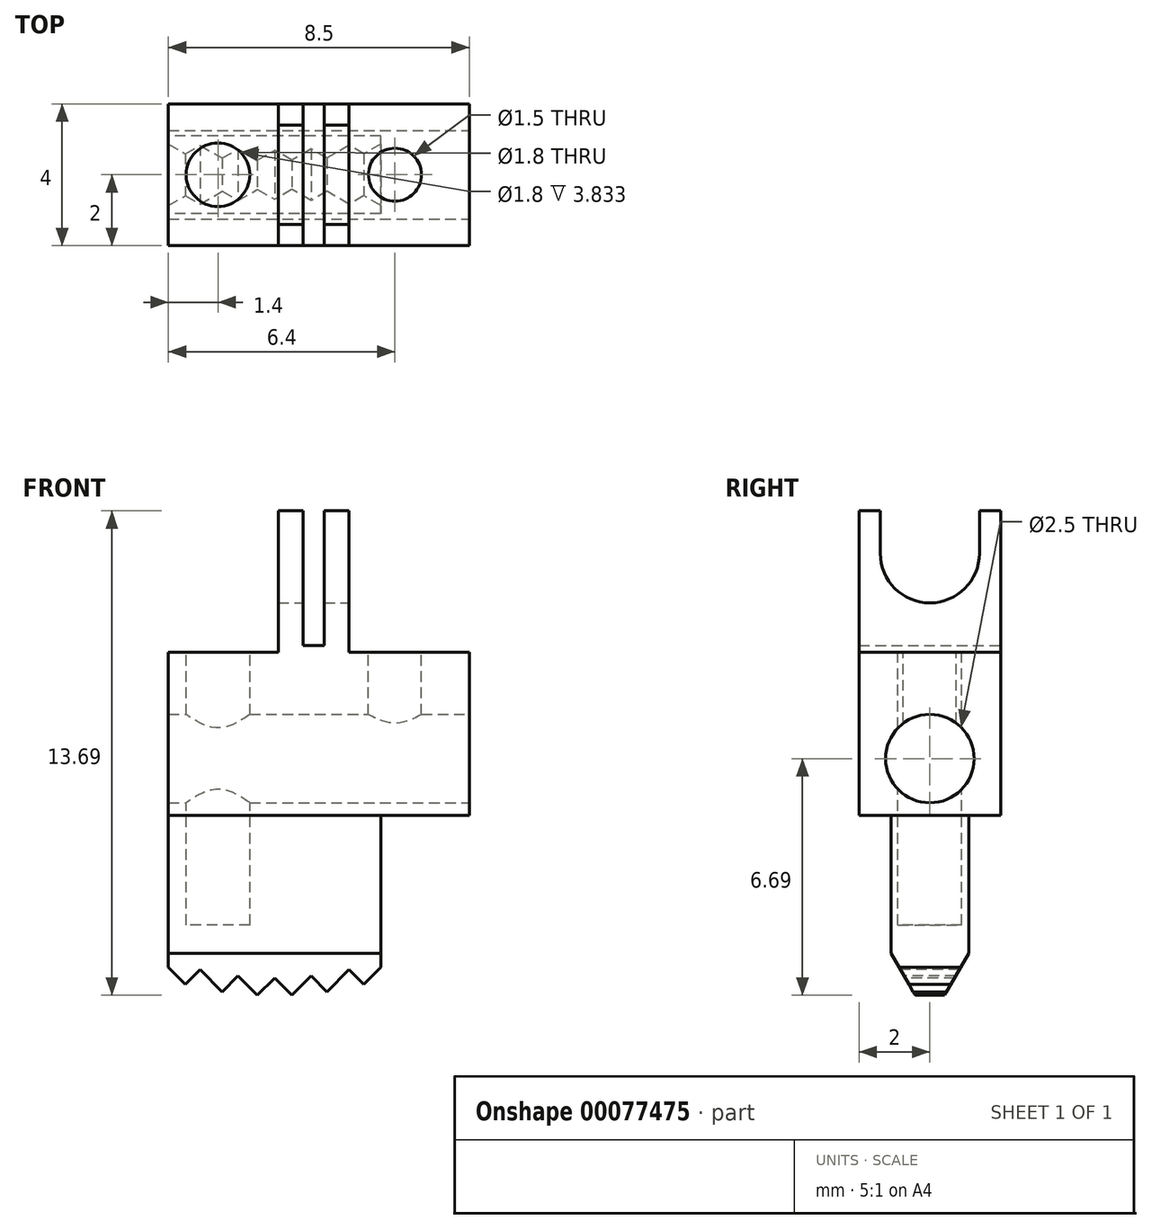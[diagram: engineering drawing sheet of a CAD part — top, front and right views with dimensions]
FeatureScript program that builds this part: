
annotation { "Feature Type Name" : "Feature", "Feature Type Description" : "" }
export const myFeature = defineFeature(function(context is Context, id is Id, definition is map)
    precondition{}
    {
        {
            var Q0;
            Q0=qCreatedBy(makeId("Front.planeOp"),FACE);
            var sketch = newSketch(context, id + "F0", { "sketchPlane" : qUnion([Q0])});
            skLineSegment(sketch, "E0", {"start": v(0, 0) * mm, "end": v(-6, 0) * mm});
            skLineSegment(sketch, "E1", {"start": v(0, 0) * mm, "end": v(0, 5.1) * mm});
            skLineSegment(sketch, "E2", {"start": v(0, 5.1) * mm, "end": v(2.5, 5.1) * mm});
            skLineSegment(sketch, "E3", {"start": v(2.5, 5.1) * mm, "end": v(2.5, 9.7) * mm});
            skLineSegment(sketch, "E4", {"start": v(2.5, 9.7) * mm, "end": v(-0.9, 9.7) * mm});
            skLineSegment(sketch, "E5", {"start": v(-0.9, 9.7) * mm, "end": v(-0.9, 13.7) * mm});
            skLineSegment(sketch, "E6", {"start": v(-0.9, 13.7) * mm, "end": v(-1.6, 13.7) * mm});
            skLineSegment(sketch, "E7", {"start": v(-1.6, 13.7) * mm, "end": v(-1.6, 9.9) * mm});
            skLineSegment(sketch, "E8", {"start": v(-1.6, 9.9) * mm, "end": v(-2.2, 9.9) * mm});
            skLineSegment(sketch, "E9", {"start": v(-2.2, 9.9) * mm, "end": v(-2.2, 13.7) * mm});
            skLineSegment(sketch, "E10", {"start": v(-2.2, 13.7) * mm, "end": v(-2.9, 13.7) * mm});
            skLineSegment(sketch, "E11", {"start": v(-2.9, 13.7) * mm, "end": v(-2.9, 9.7) * mm});
            skLineSegment(sketch, "E12", {"start": v(-2.9, 9.7) * mm, "end": v(-6, 9.7) * mm});
            skLineSegment(sketch, "E13", {"start": v(-6, 9.7) * mm, "end": v(-6, 0) * mm});
            skLineSegment(sketch, "E14", {"start": v(-3, 0) * mm, "end": v(-3, 10) * mm, "construction": true});
            skCircle(sketch, "E15", {"center": v(-3, 10) * mm, "radius": 10 * mm, "construction": true});
            skLineSegment(sketch, "E16", {"start": v(0, 5.1) * mm, "end": v(-6, 5.1) * mm});
            skSolve(sketch);
        }
        {
            var Q0;
            Q0=makeQuery(id+"F0.imprint","IMPRINT",FACE,{"disambiguationData":[TD([[makeQuery(id+"F0.imprint","IMPRINT",EDGE,{"derivedFrom":sQuery(id+"F0.wireOp",EDGE,"E2")}),1.0]])]});
            extrude(context, id + "F1", {"entities" : qUnion([Q0]), "depth" : 4 * mm, "symmetric" : true});
        }
        {
            var Q0;
            {var subQ2=sQuery(id+"F0.wireOp",EDGE,"E0");Q0=makeQuery(id+"F0.imprint","IMPRINT",FACE,{"disambiguationData":[TD([[makeQuery(id+"F0.imprint","IMPRINT",EDGE,{"derivedFrom":subQ2}),-1.0]])]});}
            extrude(context, id + "F2", {"entities" : qUnion([Q0]), "operationType" : NewBodyOperationType.ADD, "depth" : 2.2 * mm, "symmetric" : true});
        }
        {
            var Q0;
            Q0=makeQuery(id+"F1.opExtrude","SWEPT_FACE",FACE,{"disambiguationData":[OSD([sQuery(id+"F0.wireOp",EDGE,"E5")])]});
            var sketch = newSketch(context, id + "F3", { "sketchPlane" : qUnion([Q0])});
            skLineSegment(sketch, "E17", {"start": v(2, 11.1) * mm, "end": v(-2, 11.1) * mm, "construction": true});
            skArc(sketch, "E18", {"start": v(-1.4, 12.5) * mm, "mid": v(0, 11.1) * mm, "end": v(1.4, 12.5) * mm});
            skLineSegment(sketch, "E19", {"start": v(-1.4, 12.5) * mm, "end": v(-1.4, 13.9) * mm});
            skLineSegment(sketch, "E20", {"start": v(-1.4, 13.9) * mm, "end": v(1.4, 13.9) * mm});
            skLineSegment(sketch, "E21", {"start": v(1.4, 13.9) * mm, "end": v(1.4, 12.5) * mm});
            skSolve(sketch);
        }
        {
            var Q0;
            {var subQ5=sQuery(id+"F3.wireOp",EDGE,"E20");Q0=makeQuery(id+"F3.imprint","IMPRINT",FACE,{"disambiguationData":[TD([[makeQuery(id+"F3.imprint","IMPRINT",EDGE,{"derivedFrom":subQ5}),-1.0]])]});}
            var Q1;
            {var subQ5=sQuery(id+"F3.wireOp",EDGE,"E18");Q1=makeQuery(id+"F3.imprint","IMPRINT",FACE,{"disambiguationData":[TD([[makeQuery(id+"F3.imprint","IMPRINT",EDGE,{"derivedFrom":subQ5}),1.0]])]});}
            extrude(context, id + "F4", {"entities" : qUnion([Q0, Q1]), "operationType" : NewBodyOperationType.REMOVE, "oppositeDirection" : true, "depth" : 2 * mm});
        }
        {
            var Q0;
            Q0=makeQuery(id+"F1.opExtrude","SWEPT_FACE",FACE,{"disambiguationData":[OSD([sQuery(id+"F0.wireOp",EDGE,"E3")])]});
            var sketch = newSketch(context, id + "F5", { "sketchPlane" : qUnion([Q0])});
            skLineSegment(sketch, "E22", {"start": v(0, 9.7) * mm, "end": v(0, 6.7) * mm, "construction": true});
            skCircle(sketch, "E23", {"center": v(0, 6.7) * mm, "radius": 1.25 * mm});
            skSolve(sketch);
        }
        {
            var Q0;
            Q0=makeQuery(id+"F5.imprint","IMPRINT",FACE,{"disambiguationData":[TD([[makeQuery(id+"F5.imprint","IMPRINT",EDGE,{"derivedFrom":sQuery(id+"F5.wireOp",EDGE,"E23")}),1.0]])]});
            extrude(context, id + "F6", {"entities" : qUnion([Q0]), "operationType" : NewBodyOperationType.REMOVE, "oppositeDirection" : true, "depth" : 8.5 * mm});
        }
        {
            var Q0;
            Q0=makeQuery(id+"F1.opExtrude","SWEPT_FACE",FACE,{"disambiguationData":[OSD([sQuery(id+"F0.wireOp",EDGE,"E4")])]});
            var sketch = newSketch(context, id + "F7", { "sketchPlane" : qUnion([Q0])});
            skCircle(sketch, "E24", {"center": v(0.4, 0) * mm, "radius": 0.75 * mm});
            skSolve(sketch);
        }
        {
            var Q0;
            Q0=makeQuery(id+"F7.imprint","IMPRINT",FACE,{"disambiguationData":[TD([[makeQuery(id+"F7.imprint","IMPRINT",EDGE,{"derivedFrom":sQuery(id+"F7.wireOp",EDGE,"E24")}),1.0]])]});
            extrude(context, id + "F8", {"entities" : qUnion([Q0]), "operationType" : NewBodyOperationType.REMOVE, "oppositeDirection" : true, "depth" : 3 * mm});
        }
        {
            var Q0;
            Q0=makeQuery(id+"F1.opExtrude","SWEPT_FACE",FACE,{"disambiguationData":[OSD([sQuery(id+"F0.wireOp",EDGE,"E12")])]});
            var sketch = newSketch(context, id + "F9", { "sketchPlane" : qUnion([Q0])});
            skLineSegment(sketch, "E25", {"start": v(-4.6, 2) * mm, "end": v(-4.6, -2) * mm, "construction": true});
            skCircle(sketch, "E26", {"center": v(-4.6, 0) * mm, "radius": 0.9 * mm});
            skSolve(sketch);
        }
        {
            var Q0;
            Q0=makeQuery(id+"F9.imprint","IMPRINT",FACE,{"disambiguationData":[TD([[makeQuery(id+"F9.imprint","IMPRINT",EDGE,{"derivedFrom":sQuery(id+"F9.wireOp",EDGE,"E26")}),1.0]])]});
            extrude(context, id + "F10", {"entities" : qUnion([Q0]), "operationType" : NewBodyOperationType.REMOVE, "oppositeDirection" : true, "depth" : 7.7 * mm});
        }
        {
            var Q0;
            Q0=makeQuery(id+"F2.opExtrude","CAP_EDGE",EDGE,{"disambiguationData":[OSD([sQuery(id+"F0.wireOp",EDGE,"E0")])],"isStart":false});
            var Q1;
            Q1=makeQuery(id+"F2.opExtrude","CAP_EDGE",EDGE,{"disambiguationData":[OSD([sQuery(id+"F0.wireOp",EDGE,"E0")])],"isStart":true});
            chamfer(context, id + "F11", {"entities" : qUnion([Q0, Q1]), "chamferType" : ChamferType.OFFSET_ANGLE, "width" : 1.2 * mm, "oppositeDirection" : true, "angle" : 30 * degree, "tangentPropagation" : true});
        }
        {
            var Q0;
            Q0=qCreatedBy(makeId("Front.planeOp"),FACE);
            var sketch = newSketch(context, id + "F12", { "sketchPlane" : qUnion([Q0])});
            skCircle(sketch, "E27", {"center": v(-3, 10) * mm, "radius": 10 * mm, "construction": true});
            skPoint(sketch, "E28", {"position": v(-3, 0) * mm});
            skCircle(sketch, "E29", {"center": v(-3, 10) * mm, "radius": 9.5 * mm, "construction": true});
            skLineSegment(sketch, "E30", {"start": v(-3, 0.5) * mm, "end": v(-3.49, 0.01) * mm});
            skLineSegment(sketch, "E31", {"start": v(-3, 0.5) * mm, "end": v(-2.51, 0.01) * mm});
            skLineSegment(sketch, "E32", {"start": v(-3.49, 0.01) * mm, "end": v(-4.03, 0.56) * mm});
            skLineSegment(sketch, "E33", {"start": v(-4.03, 0.56) * mm, "end": v(-4.48, 0.1) * mm});
            skLineSegment(sketch, "E34", {"start": v(-4.48, 0.1) * mm, "end": v(-5.1, 0.74) * mm});
            skLineSegment(sketch, "E35", {"start": v(-5.1, 0.74) * mm, "end": v(-5.52, 0.32) * mm});
            skLineSegment(sketch, "E36", {"start": v(-5.52, 0.32) * mm, "end": v(-6, 0.8) * mm});
            skLineSegment(sketch, "E37", {"start": v(-6, 0.8) * mm, "end": v(-6, 0) * mm});
            skLineSegment(sketch, "E38", {"start": v(-6, 0) * mm, "end": v(0, 0) * mm});
            skLineSegment(sketch, "E39", {"start": v(0, 0) * mm, "end": v(0, 0.8) * mm});
            skLineSegment(sketch, "E40", {"start": v(-2.51, 0.01) * mm, "end": v(-1.97, 0.56) * mm});
            skLineSegment(sketch, "E41", {"start": v(-1.97, 0.56) * mm, "end": v(-1.52, 0.1) * mm});
            skLineSegment(sketch, "E42", {"start": v(-1.52, 0.1) * mm, "end": v(-0.9, 0.74) * mm});
            skLineSegment(sketch, "E43", {"start": v(-0.9, 0.74) * mm, "end": v(-0.48, 0.32) * mm});
            skLineSegment(sketch, "E44", {"start": v(-0.48, 0.32) * mm, "end": v(0, 0.8) * mm});
            skSolve(sketch);
        }
        {
            var Q0;
            Q0=makeQuery(id+"F12.imprint","IMPRINT",FACE,{"disambiguationData":[TD([[makeQuery(id+"F12.imprint","IMPRINT",EDGE,{"derivedFrom":sQuery(id+"F12.wireOp",EDGE,"E30")}),1.0]])]});
            extrude(context, id + "F13", {"entities" : qUnion([Q0]), "operationType" : NewBodyOperationType.REMOVE, "oppositeDirection" : true, "depth" : 25 * mm, "symmetric" : true});
        }
    });
